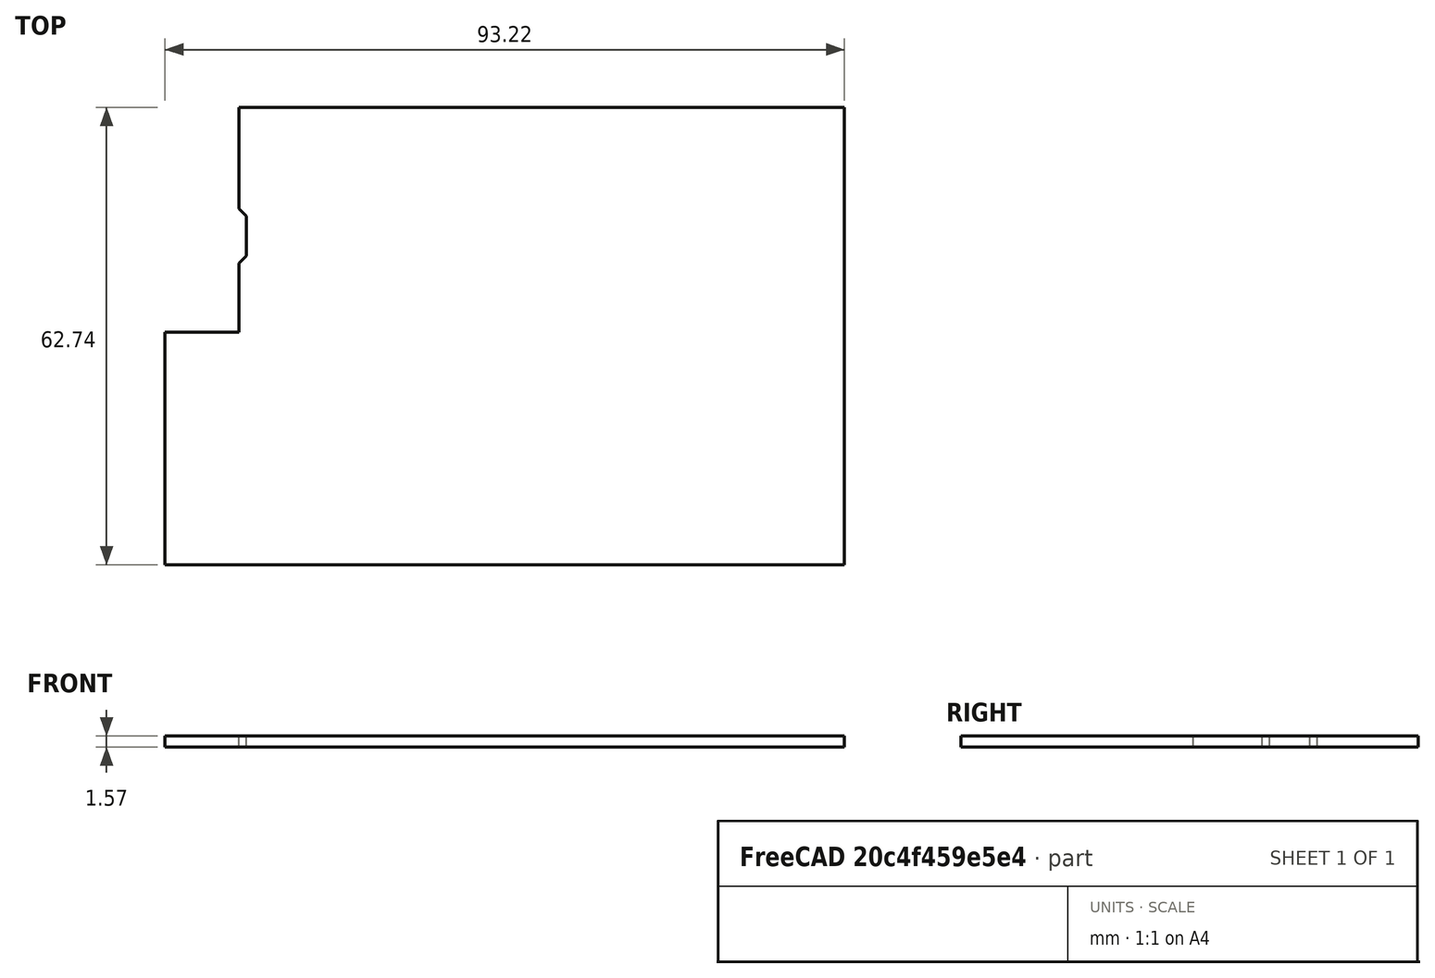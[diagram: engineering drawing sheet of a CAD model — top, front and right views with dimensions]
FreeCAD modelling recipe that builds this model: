
FCSTD DOCUMENT  (FreeCAD 0.18R16111 (Git))
Label: pololu-motor-power-board
License: All rights reserved
LicenseURL: http://en.wikipedia.org/wiki/All_rights_reserved
objects: Sketcher::SketchObject×2, Part::Extrusion×1
note: 3 computed .brp shape members not serialized (recipe doc carries the construction recipe); baked Part::Feature solids carry a one-line shape summary decoded from their .brp

FEATURE [Sketcher::SketchObject] Sketch126
  sketch-geometry (10):
    g0: LineSegment StartX=0 StartY=0 StartZ=0 EndX=93.22 EndY=0 EndZ=0
    g1: LineSegment StartX=93.22 StartY=0 StartZ=0 EndX=93.22 EndY=62.74 EndZ=0
    g2: LineSegment StartX=93.22 StartY=62.74 StartZ=0 EndX=10.16 EndY=62.74 EndZ=0
    g3: LineSegment StartX=10.16 StartY=62.74 StartZ=0 EndX=10.16 EndY=48.89 EndZ=0
    g4: LineSegment StartX=10.16 StartY=48.89 StartZ=0 EndX=11.18 EndY=47.8765 EndZ=0
    g5: LineSegment StartX=11.18 StartY=47.8765 StartZ=0 EndX=11.18 EndY=42.3665 EndZ=0
    g6: LineSegment StartX=11.18 StartY=42.3665 StartZ=0 EndX=10.16 EndY=41.35 EndZ=0
    g7: LineSegment StartX=10.16 StartY=41.35 StartZ=0 EndX=10.16 EndY=31.88 EndZ=0
    g8: LineSegment StartX=10.16 StartY=31.88 StartZ=0 EndX=0 EndY=31.88 EndZ=0
    g9: LineSegment StartX=0 StartY=31.88 StartZ=0 EndX=0 EndY=0 EndZ=0
  constraints (29):
    c: Horizontal(g0)
    c: Coincident(g0,g1)
    c: Vertical(g1)
    c: Coincident(g1,g2)
    c: Horizontal(g2)
    c: Coincident(g2,g3)
    c: Vertical(g3)
    c: Coincident(g3,g4)
    c: Coincident(g4,g5)
    c: Vertical(g5)
    c: Coincident(g5,g6)
    c: Coincident(g6,g7)
    c: Vertical(g7)
    c: Coincident(g7,g8)
    c: Horizontal(g8)
    c: Coincident(g8,g9)
    c: Vertical(g9)
    c: Coincident(g9,g0)
    c: Distance(g9) = 31.88
    c: Distance(g0) = 93.22
    c: Distance(g1) = 62.74
    c: Distance(g2) = 83.06
    c: Distance(g3) = 13.85
    c: Distance(g7) = 9.47
    c: Distance(g8) = 10.16
    c: DistanceX(g3,g4) = 1.02
    c: Distance(g5) = 5.51
    c: Distance(g6) = 1.44
    c: Coincident(g0,g-1)
FEATURE [Part::Extrusion] Extrude
  Base = -> Sketch126
  Dir = (0,0,1)
  DirMode = 2
  FaceMakerClass = Part::FaceMakerBullseye
  LengthFwd = 1.5748
  LengthRev = 0
  Solid = true
  Symmetric = false
FEATURE [Sketcher::SketchObject] Sketch
  sketch-geometry (1):
    g0: Circle CenterX=87.6128 CenterY=3.95604 CenterZ=0 NormalX=0 NormalY=0 NormalZ=1 AngleXU=0 Radius=3.57807
